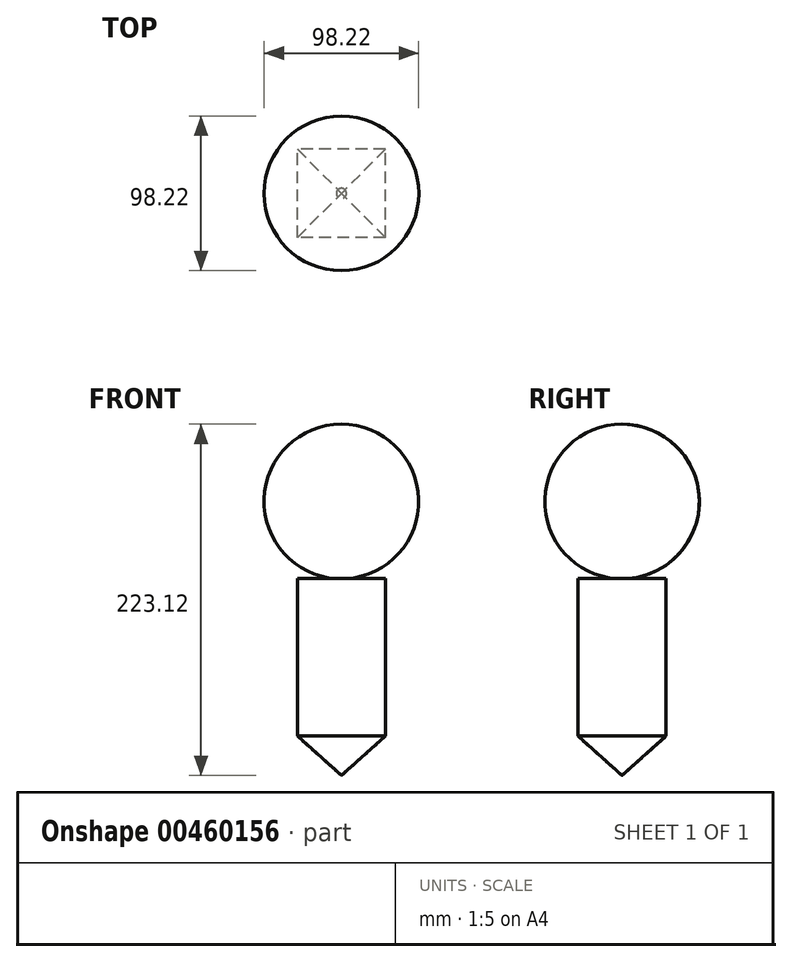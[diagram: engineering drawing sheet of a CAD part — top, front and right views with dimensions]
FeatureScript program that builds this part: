
annotation { "Feature Type Name" : "Feature", "Feature Type Description" : "" }
export const myFeature = defineFeature(function(context is Context, id is Id, definition is map)
    precondition{}
    {
        {
            var Q0;
            Q0=qCreatedBy(makeId("Top.planeOp"),FACE);
            var sketch = newSketch(context, id + "F0", { "sketchPlane" : qUnion([Q0])});
            skLineSegment(sketch, "E0.bottom", {"start": v(27.9, -28.01) * mm, "end": v(-27.9, -28.01) * mm});
            skLineSegment(sketch, "E0.top", {"start": v(27.9, 28.01) * mm, "end": v(-27.9, 28.01) * mm});
            skLineSegment(sketch, "E0.left", {"start": v(27.9, -28.01) * mm, "end": v(27.9, 28.01) * mm});
            skLineSegment(sketch, "E0.right", {"start": v(-27.9, -28.01) * mm, "end": v(-27.9, 28.01) * mm});
            skPoint(sketch, "E0.middle", {"position": v(0, 0) * mm});
            skSolve(sketch);
        }
        {
            var Q0;
            Q0=makeQuery(id+"F0.imprint","IMPRINT",FACE,{"disambiguationData":[TD([[makeQuery(id+"F0.imprint","IMPRINT",EDGE,{"derivedFrom":sQuery(id+"F0.wireOp",EDGE,"E0.bottom")}),-1.0]])]});
            extrude(context, id + "F1", {"entities" : qUnion([Q0]), "endBound" : BoundingType.SYMMETRIC, "depth" : 100 * mm});
        }
        {
            var Q0;
            Q0=qCreatedBy(makeId("Right.planeOp"),FACE);
            var sketch = newSketch(context, id + "F2", { "sketchPlane" : qUnion([Q0])});
            skCircle(sketch, "E1", {"center": v(0, 99) * mm, "radius": 49.11 * mm});
            skLineSegment(sketch, "E2", {"start": v(0, 49.9) * mm, "end": v(0, 148.12) * mm});
            skSolve(sketch);
        }
        {
            var Q0;
            {var subQ0=sQuery(id+"F2.wireOp",EDGE,"E2");Q0=makeQuery(id+"F2.imprint","IMPRINT",FACE,{"disambiguationData":[TD([[makeQuery(id+"F2.imprint","IMPRINT",EDGE,{"derivedFrom":subQ0}),1.0]])]});}
            var Q1;
            Q1=sQuery(id+"F2.wireOp",EDGE,"E2");
            revolve(context, id + "F3", {"operationType" : NewBodyOperationType.ADD, "entities" : qUnion([Q0]), "axis" : qUnion([Q1]), "revolveType" : RevolveType.FULL});
        }
        {
            var Q0;
            Q0=qCreatedBy(makeId("Top.planeOp"),FACE);
            cPlane(context, id + "F4", {"entities" : qUnion([Q0]), "cplaneType" : CPlaneType.OFFSET, "offset" : 75 * mm, "oppositeDirection" : true, "width" : 150 * mm, "height" : 150 * mm});
        }
        {
            var Q0;
            Q0=qCreatedBy(id+"F4.planeOp",FACE);
            var sketch = newSketch(context, id + "F5", { "sketchPlane" : qUnion([Q0])});
            skCircle(sketch, "E3", {"center": v(0, 0) * mm, "radius": 0.01 * mm});
            skSolve(sketch);
        }
        {
            var Q1;
            Q1=makeQuery(id+"F1.opExtrude","CAP_FACE",FACE,{"disambiguationData":[OSD([sQuery(id+"F0.wireOp",EDGE,"E0.bottom"),sQuery(id+"F0.wireOp",EDGE,"E0.top"),sQuery(id+"F0.wireOp",EDGE,"E0.left"),sQuery(id+"F0.wireOp",EDGE,"E0.right")])],"isStart":true});
            var Q2;
            Q2=makeQuery(id+"F5.imprint","IMPRINT",FACE,{"disambiguationData":[TD([[makeQuery(id+"F5.imprint","IMPRINT",EDGE,{"derivedFrom":sQuery(id+"F5.wireOp",EDGE,"E3")}),1.0]])]});
            loft(context, id + "F6", {"operationType" : NewBodyOperationType.ADD, "sheetProfilesArray" : [{ "sheetProfileEntities" : qUnion([Q1]) }, { "sheetProfileEntities" : qUnion([Q2]) }]});
        }
    });
